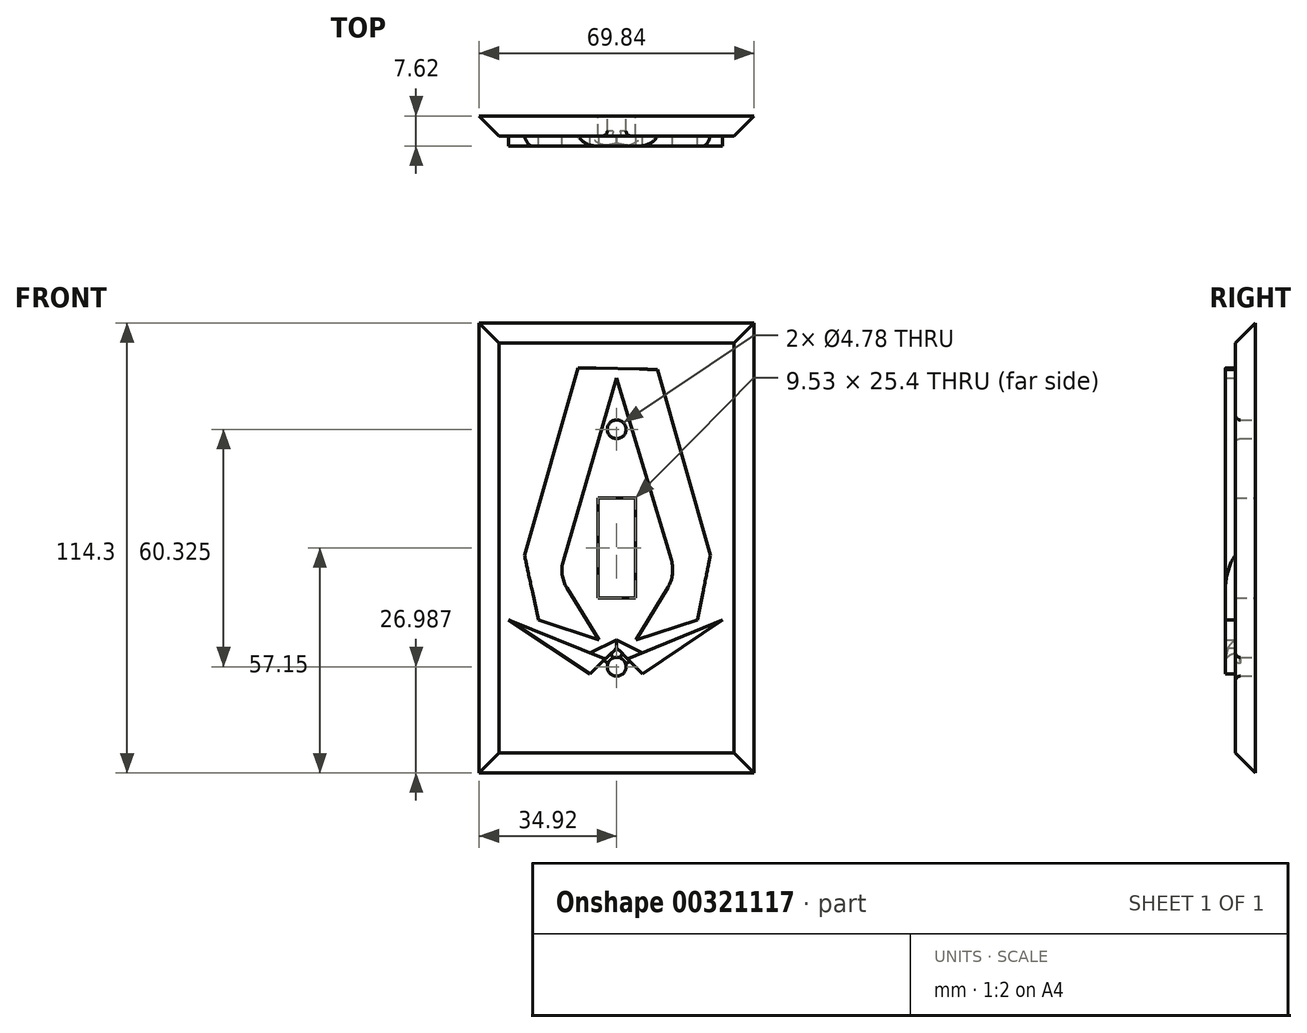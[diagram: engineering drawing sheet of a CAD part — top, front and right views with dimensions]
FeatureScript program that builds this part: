
annotation { "Feature Type Name" : "Feature", "Feature Type Description" : "" }
export const myFeature = defineFeature(function(context is Context, id is Id, definition is map)
    precondition{}
    {
        {
            var Q0;
            Q0=qCreatedBy(makeId("Front.planeOp"),FACE);
            var sketch = newSketch(context, id + "F0", { "sketchPlane" : qUnion([Q0])});
            skLineSegment(sketch, "E0.bottom", {"start": v(34.92, 57.15) * mm, "end": v(-34.93, 57.15) * mm});
            skLineSegment(sketch, "E0.top", {"start": v(34.93, -57.15) * mm, "end": v(-34.92, -57.15) * mm});
            skLineSegment(sketch, "E0.left", {"start": v(34.92, 57.15) * mm, "end": v(34.93, -57.15) * mm});
            skLineSegment(sketch, "E0.right", {"start": v(-34.93, 57.15) * mm, "end": v(-34.92, -57.15) * mm});
            skPoint(sketch, "E0.middle", {"position": v(0, 0) * mm});
            skLineSegment(sketch, "E1.bottom", {"start": v(4.76, 12.7) * mm, "end": v(-4.76, 12.7) * mm});
            skLineSegment(sketch, "E1.top", {"start": v(4.76, -12.7) * mm, "end": v(-4.76, -12.7) * mm});
            skLineSegment(sketch, "E1.left", {"start": v(4.76, 12.7) * mm, "end": v(4.76, -12.7) * mm});
            skLineSegment(sketch, "E1.right", {"start": v(-4.76, 12.7) * mm, "end": v(-4.76, -12.7) * mm});
            skCircle(sketch, "E2", {"center": v(0, 30.16) * mm, "radius": 2.39 * mm});
            skCircle(sketch, "E3", {"center": v(0, -30.16) * mm, "radius": 2.39 * mm});
            skSolve(sketch);
        }
        {
            var Q0;
            Q0 = qSketchRegion(id + "F0", true);
            extrude(context, id + "F1", {"entities" : qUnion([Q0]), "depth" : 5.08 * mm});
        }
        {
            var Q0;
            Q0=makeQuery(id+"F1.opExtrude","CAP_EDGE",EDGE,{"disambiguationData":[OSD([sQuery(id+"F0.wireOp",EDGE,"E0.bottom")])],"isStart":false});
            var Q1;
            Q1=makeQuery(id+"F1.opExtrude","CAP_EDGE",EDGE,{"disambiguationData":[OSD([sQuery(id+"F0.wireOp",EDGE,"E0.left")])],"isStart":false});
            var Q2;
            Q2=makeQuery(id+"F1.opExtrude","CAP_EDGE",EDGE,{"disambiguationData":[OSD([sQuery(id+"F0.wireOp",EDGE,"E0.top")])],"isStart":false});
            var Q3;
            Q3=makeQuery(id+"F1.opExtrude","CAP_EDGE",EDGE,{"disambiguationData":[OSD([sQuery(id+"F0.wireOp",EDGE,"E0.right")])],"isStart":false});
            chamfer(context, id + "F2", {"entities" : qUnion([Q0, Q1, Q2, Q3]), "width" : 5.08 * mm, "tangentPropagation" : true});
        }
        {
            var Q0;
            Q0=makeQuery(id+"F1.opExtrude","CAP_FACE",FACE,{"disambiguationData":[OSD([sQuery(id+"F0.wireOp",EDGE,"E0.bottom"),sQuery(id+"F0.wireOp",EDGE,"E0.top"),sQuery(id+"F0.wireOp",EDGE,"E0.left"),sQuery(id+"F0.wireOp",EDGE,"E0.right"),sQuery(id+"F0.wireOp",EDGE,"E1.bottom"),sQuery(id+"F0.wireOp",EDGE,"E1.top"),sQuery(id+"F0.wireOp",EDGE,"E1.left"),sQuery(id+"F0.wireOp",EDGE,"E1.right"),sQuery(id+"F0.wireOp",EDGE,"E2"),sQuery(id+"F0.wireOp",EDGE,"E3")])],"isStart":false});
            var sketch = newSketch(context, id + "F3", { "sketchPlane" : qUnion([Q0])});
            skPoint(sketch, "E4.endSnap0", {"position": v(0, -52.07) * mm});
            skLineSegment(sketch, "E5", {"start": v(-9.78, 45.78) * mm, "end": v(10.42, 45.36) * mm});
            skLineSegment(sketch, "E6", {"start": v(23.79, -1.9) * mm, "end": v(20.49, -18.23) * mm});
            skLineSegment(sketch, "E7", {"start": v(-23.4, -1.9) * mm, "end": v(-19.9, -18.23) * mm});
            skLineSegment(sketch, "E8", {"start": v(-13.57, -3.2) * mm, "end": v(0, 43.21) * mm});
            skLineSegment(sketch, "E9", {"start": v(13.87, -3.08) * mm, "end": v(0, 43.21) * mm});
            skPoint(sketch, "E10.startSnap0", {"position": v(0, -12.7) * mm});
            skPoint(sketch, "E11.visualSharp", {"position": v(16.03, -10.3) * mm});
            skArc(sketch, "E11.filletArc", {"start": v(12.96, -10.05) * mm, "mid": v(14.16, -6.66) * mm, "end": v(13.87, -3.08) * mm});
            skPoint(sketch, "E12.visualSharp", {"position": v(-15.65, -10.3) * mm});
            skArc(sketch, "E12.filletArc", {"start": v(-13.57, -3.2) * mm, "mid": v(-13.84, -6.78) * mm, "end": v(-12.64, -10.16) * mm});
            skLineSegment(sketch, "E13", {"start": v(-12.64, -10.16) * mm, "end": v(-4.52, -23.35) * mm});
            skLineSegment(sketch, "E14", {"start": v(-4.52, -23.35) * mm, "end": v(-19.9, -18.23) * mm});
            skLineSegment(sketch, "E15", {"start": v(12.96, -10.05) * mm, "end": v(4.86, -23.35) * mm});
            skLineSegment(sketch, "E16", {"start": v(4.86, -23.35) * mm, "end": v(20.49, -18.23) * mm});
            skLineSegment(sketch, "E17", {"start": v(10.42, 45.36) * mm, "end": v(23.79, -1.9) * mm});
            skLineSegment(sketch, "E18", {"start": v(-9.78, 45.78) * mm, "end": v(-23.4, -1.9) * mm});
            skLineSegment(sketch, "E19", {"start": v(0, -23.35) * mm, "end": v(6.55, -26.66) * mm});
            skLineSegment(sketch, "E20", {"start": v(6.55, -32.05) * mm, "end": v(0, -25.38) * mm});
            skLineSegment(sketch, "E21", {"start": v(0, -25.38) * mm, "end": v(-6.8, -32.05) * mm});
            skLineSegment(sketch, "E22", {"start": v(-6.8, -26.66) * mm, "end": v(0, -23.35) * mm});
            skLineSegment(sketch, "E23", {"start": v(-6.8, -26.66) * mm, "end": v(-27.43, -18.23) * mm});
            skLineSegment(sketch, "E24", {"start": v(-27.43, -18.23) * mm, "end": v(-6.8, -32.05) * mm});
            skLineSegment(sketch, "E25", {"start": v(6.55, -26.66) * mm, "end": v(26.85, -18.23) * mm});
            skLineSegment(sketch, "E26", {"start": v(26.85, -18.23) * mm, "end": v(6.55, -32.05) * mm});
            skSolve(sketch);
        }
        {
            var Q0;
            Q0 = qSketchRegion(id + "F3", true);
            extrude(context, id + "F4", {"entities" : qUnion([Q0]), "operationType" : NewBodyOperationType.ADD, "depth" : 2.54 * mm});
        }
        {
            var Q0;
            Q0=makeQuery(id+"F4.opExtrude","CAP_EDGE",EDGE,{"disambiguationData":[OSD([sQuery(id+"F3.wireOp",EDGE,"E18")])],"isStart":false});
            var Q1;
            Q1=makeQuery(id+"F4.opExtrude","CAP_EDGE",EDGE,{"disambiguationData":[OSD([sQuery(id+"F3.wireOp",EDGE,"E17")])],"isStart":false});
            var Q2;
            Q2=makeQuery(id+"F4.opExtrude","CAP_EDGE",EDGE,{"disambiguationData":[OSD([sQuery(id+"F3.wireOp",EDGE,"E19")])],"isStart":false});
            var Q3;
            Q3=makeQuery(id+"F4.opExtrude","CAP_EDGE",EDGE,{"disambiguationData":[OSD([sQuery(id+"F3.wireOp",EDGE,"E22")])],"isStart":false});
            fillet(context, id + "F5", {"entities" : qUnion([Q0, Q1, Q2, Q3]), "radius" : 5.08 * mm, "tangentPropagation" : true, "allowEdgeOverflow" : false});
        }
        {
            var Q0;
            Q0=makeQuery(id+"F1.opExtrude","CAP_EDGE",EDGE,{"disambiguationData":[OSD([sQuery(id+"F0.wireOp",EDGE,"E2")])],"isStart":false});
            var Q1;
            Q1=makeQuery(id+"F1.opExtrude","CAP_EDGE",EDGE,{"disambiguationData":[OSD([sQuery(id+"F0.wireOp",EDGE,"E3")])],"isStart":false});
            fillet(context, id + "F6", {"entities" : qUnion([Q0, Q1]), "radius" : 1.27 * mm, "tangentPropagation" : true, "allowEdgeOverflow" : false});
        }
    });
